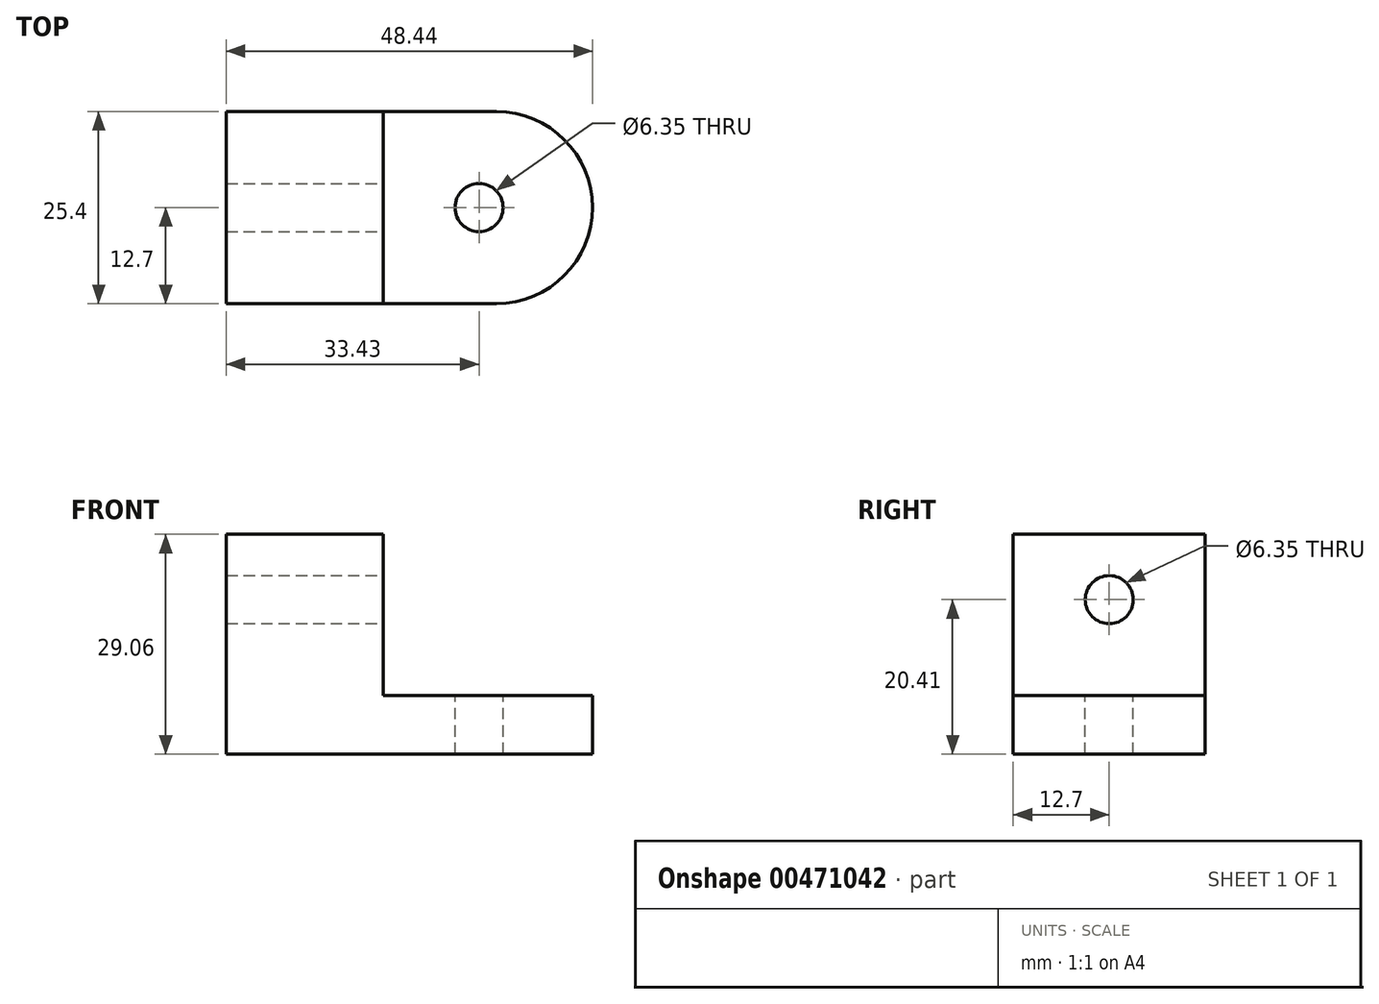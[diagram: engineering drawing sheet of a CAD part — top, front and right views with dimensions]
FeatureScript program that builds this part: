
annotation { "Feature Type Name" : "Feature", "Feature Type Description" : "" }
export const myFeature = defineFeature(function(context is Context, id is Id, definition is map)
    precondition{}
    {
        {
            var Q0;
            Q0=qCreatedBy(makeId("Front.planeOp"),FACE);
            var sketch = newSketch(context, id + "F0", { "sketchPlane" : qUnion([Q0])});
            skLineSegment(sketch, "E0", {"start": v(0, 0) * mm, "end": v(0, 21.35) * mm});
            skLineSegment(sketch, "E1", {"start": v(0, 21.35) * mm, "end": v(-20.73, 21.35) * mm});
            skLineSegment(sketch, "E2", {"start": v(-20.73, 21.35) * mm, "end": v(-20.73, -7.71) * mm});
            skLineSegment(sketch, "E3", {"start": v(-20.73, -7.71) * mm, "end": v(27.71, -7.71) * mm});
            skLineSegment(sketch, "E4", {"start": v(27.71, -7.71) * mm, "end": v(27.71, 0) * mm});
            skLineSegment(sketch, "E5", {"start": v(27.71, 0) * mm, "end": v(0, 0) * mm});
            skSolve(sketch);
        }
        {
            var Q0;
            Q0=makeQuery(id+"F0.imprint","IMPRINT",FACE,{"disambiguationData":[TD([[makeQuery(id+"F0.imprint","IMPRINT",EDGE,{"derivedFrom":sQuery(id+"F0.wireOp",EDGE,"E0")}),1.0]])]});
            extrude(context, id + "F1", {"entities" : qUnion([Q0]), "endBound" : BoundingType.SYMMETRIC, "depth" : 25.4 * mm});
        }
        {
            var Q0;
            Q0=makeQuery(id+"F1.opExtrude","CAP_EDGE",EDGE,{"disambiguationData":[OSD([sQuery(id+"F0.wireOp",EDGE,"E4")])],"isStart":false});
            var Q1;
            Q1=makeQuery(id+"F1.opExtrude","CAP_EDGE",EDGE,{"disambiguationData":[OSD([sQuery(id+"F0.wireOp",EDGE,"E4")])],"isStart":true});
            fillet(context, id + "F2", {"entities" : qUnion([Q0, Q1]), "radius" : 12.7 * mm, "tangentPropagation" : true, "allowEdgeOverflow" : false});
        }
        {
            var Q0;
            Q0=makeQuery(id+"F1.opExtrude","SWEPT_FACE",FACE,{"disambiguationData":[OSD([sQuery(id+"F0.wireOp",EDGE,"E5")])]});
            var sketch = newSketch(context, id + "F3", { "sketchPlane" : qUnion([Q0])});
            skCircle(sketch, "E6", {"center": v(12.7, 0) * mm, "radius": 3.18 * mm});
            skSolve(sketch);
        }
        {
            var Q0;
            Q0=sQuery(id+"F3.wireOp",VERTEX,"E6.center");
            var Q1;
            Q1=makeQuery(id+"F1.opExtrude","SWEPT_BODY",BODY,{"disambiguationData":[OSD([sQuery(id+"F0.wireOp",EDGE,"E0"),sQuery(id+"F0.wireOp",EDGE,"E1"),sQuery(id+"F0.wireOp",EDGE,"E2"),sQuery(id+"F0.wireOp",EDGE,"E3"),sQuery(id+"F0.wireOp",EDGE,"E4"),sQuery(id+"F0.wireOp",EDGE,"E5")])]});
            hole(context, id + "F4", {"style" : HoleStyle.SIMPLE, "endStyle" : HoleEndStyle.THROUGH, "holeDiameter" : 6.35 * mm, "isTappedThrough" : true, "tappedDepth" : 12.7 * mm, "tapClearance" : 3, "locations" : qUnion([Q0]), "scope" : qUnion([Q1])});
        }
        {
            var Q0;
            Q0=makeQuery(id+"F1.opExtrude","SWEPT_FACE",FACE,{"disambiguationData":[OSD([sQuery(id+"F0.wireOp",EDGE,"E0")])]});
            var sketch = newSketch(context, id + "F5", { "sketchPlane" : qUnion([Q0])});
            skCircle(sketch, "E7", {"center": v(0, 12.7) * mm, "radius": 3.18 * mm});
            skSolve(sketch);
        }
        {
            var Q0;
            Q0=sQuery(id+"F5.wireOp",VERTEX,"E7.center");
            var Q1;
            Q1=makeQuery(id+"F1.opExtrude","SWEPT_BODY",BODY,{"disambiguationData":[OSD([sQuery(id+"F0.wireOp",EDGE,"E0"),sQuery(id+"F0.wireOp",EDGE,"E1"),sQuery(id+"F0.wireOp",EDGE,"E2"),sQuery(id+"F0.wireOp",EDGE,"E3"),sQuery(id+"F0.wireOp",EDGE,"E4"),sQuery(id+"F0.wireOp",EDGE,"E5")])]});
            hole(context, id + "F6", {"style" : HoleStyle.SIMPLE, "endStyle" : HoleEndStyle.THROUGH, "holeDiameter" : 6.35 * mm, "isTappedThrough" : true, "tappedDepth" : 12.7 * mm, "tapClearance" : 3, "locations" : qUnion([Q0]), "scope" : qUnion([Q1])});
        }
    });
